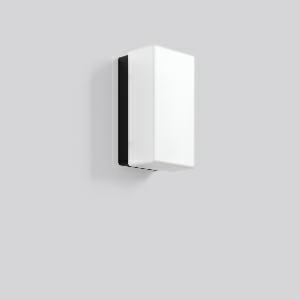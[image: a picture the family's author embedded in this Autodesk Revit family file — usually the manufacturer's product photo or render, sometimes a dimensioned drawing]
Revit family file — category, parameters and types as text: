
# Revit family: rechteck_20146_003_d4fe
name_source: partatom
category: Lighting Fixtures
units: mm (PartAtom-declared; Revit-internal decimal feet)

## family parameters
Cut with Voids When Loaded = No
Host = Face
Light Source = No
Part Type = Normal
Room Calculation Point = No
Round Connector Dimension = Use Diameter
Shared = No

## types (1)
- RECHTECK (1 x QA60/clear E27, 700 lm, 46 W, 3000)
    Apparent Load = 46 VA
    CIE Flux Codes = 34 63 85 72 42
    Color Rendering = 90
    Color Temperature = 3000
    Default Elevation = 1800 mm
    Description = Series: RECHTECK
Rectangular surface-mounted luminaire in classic design. Base: plastic. Opal glass: mouth blown, silk finish. Diffuser fastening: spring system. Suitable for Ceiling mounting, Wall (surface). IP 43 ceiling mounting, IP 44 wall mounting. 
Colour: black
Length: 220 mm
Width: 120 mm
Height: 105 mm
Lamp: A60
Number of lamps: 1
Wattage: 60 W
Socket: E27
System power: 46 W
Rated luminous flux: 300 lm
Luminous efficiency: 7 lm/W
Control gear: Converter not necessary
Protection class: II
Type of protection: IP 43
    Height = 105 mm
    Lamp = 1 x QA60/clear E27
    Lamp Light Flux = 700 lm
    Lamp Power = 46 W
    Lamp count = 1
    Length = 220 mm
    Lifetime = 3000 h
    Luminous efficacy = 6 lm/W
    Manufacturer = RZB
    ModVariant = No
    Model = 20146.003
    Mounting Place = Wall, Ceiling
    Mounting Type = Surface mounted
    Number of Poles = 1
    OnlyDefault = Yes
    Power Factor = 1
    Product Name = RECHTECK
    Product group = Surface mounted ceiling and wall luminaires
    ProductGroupID = 305
    Protection Class = Protection class II
    Protection Degree = IP 43
    RLX_Detail_Level = 1
    RLX_Emergency_Light_Flux = 0 lm
    RLX_Emergency_Type = 0
    RLX_Emergency_Type_DB = No
    RlxData = <blob elided: 20245 chars, md5=a39dd817>
    Socket = E27
    Standby Power = 0 W
    System Light Flux = 297 lm
    System Power = 46 W
    Type Comments = Product without accessories
    Type Image = 21146.003.jpg
    URL = http://relux.com
    VarID = ---
    Voltage = 230 V
    Voltage Range = 220-240 V
    Weight = 0.00 kg
    Width = 120 mm

## geometry (parser evidence)
native form markers: Blend x4, Sweep x14
no freeform markers — native parametric forms only
